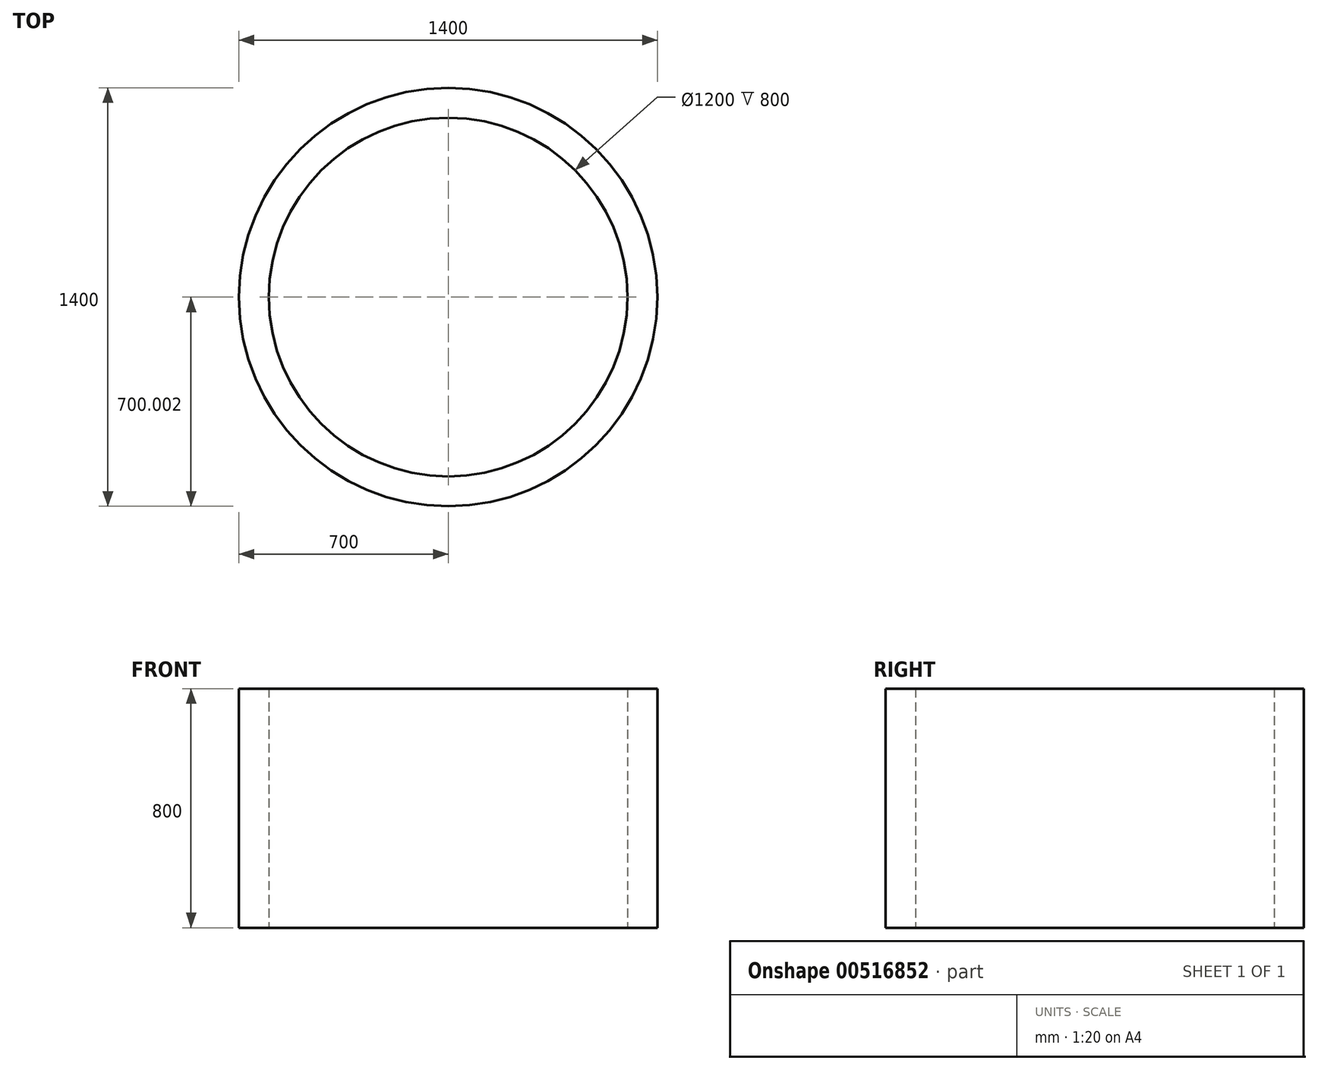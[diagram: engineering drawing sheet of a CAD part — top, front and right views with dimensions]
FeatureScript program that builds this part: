
annotation { "Feature Type Name" : "Feature", "Feature Type Description" : "" }
export const myFeature = defineFeature(function(context is Context, id is Id, definition is map)
    precondition{}
    {
        {
            var Q0;
            Q0=qCreatedBy(makeId("Top.planeOp"),FACE);
            var sketch = newSketch(context, id + "F0", { "sketchPlane" : qUnion([Q0])});
            skCircle(sketch, "E0", {"center": v(0, -1.27) * mm, "radius": 700 * mm});
            skCircle(sketch, "E1", {"center": v(0, -1.27) * mm, "radius": 600 * mm});
            skSolve(sketch);
        }
        {
            var Q0;
            Q0=makeQuery(id+"F0.imprint","IMPRINT",FACE,{"disambiguationData":[TD([[makeQuery(id+"F0.imprint","IMPRINT",EDGE,{"derivedFrom":sQuery(id+"F0.wireOp",EDGE,"E0")}),1.0]])]});
            extrude(context, id + "F1", {"entities" : qUnion([Q0]), "endBound" : BoundingType.SYMMETRIC, "depth" : 800 * mm});
        }
    });
